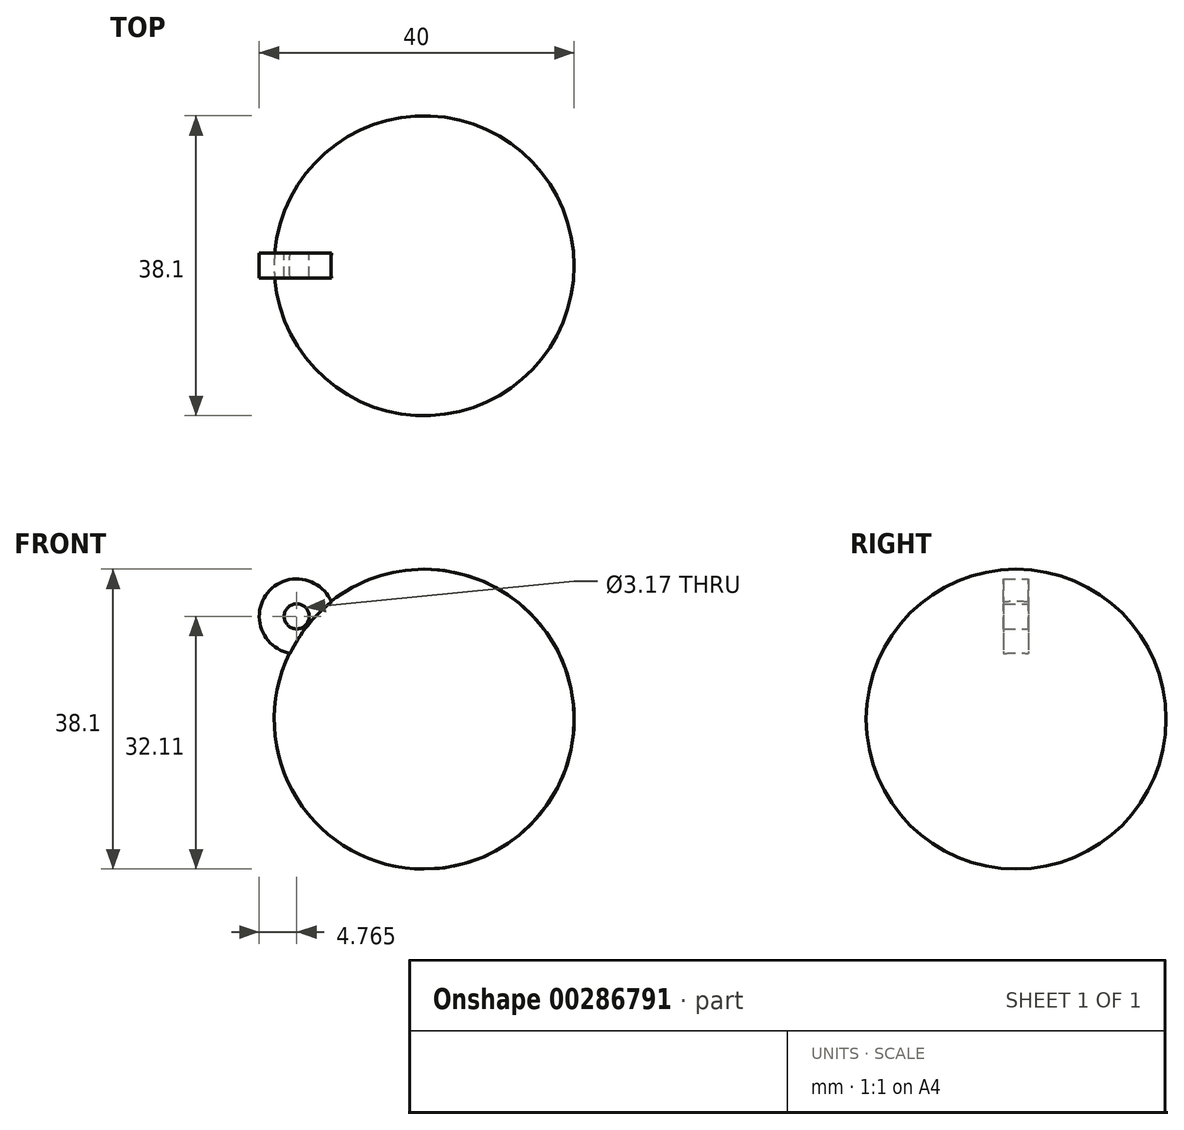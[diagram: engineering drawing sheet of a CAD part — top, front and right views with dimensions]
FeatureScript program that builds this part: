
annotation { "Feature Type Name" : "Feature", "Feature Type Description" : "" }
export const myFeature = defineFeature(function(context is Context, id is Id, definition is map)
    precondition{}
    {
        {
            var Q0;
            Q0=qCreatedBy(makeId("Front.planeOp"),FACE);
            var sketch = newSketch(context, id + "F0", { "sketchPlane" : qUnion([Q0])});
            skArc(sketch, "E0", {"start": v(0, 19.05) * mm, "mid": v(-19.05, 0) * mm, "end": v(0, -19.05) * mm});
            skLineSegment(sketch, "E1", {"start": v(0, 19.05) * mm, "end": v(0, -19.05) * mm});
            skSolve(sketch);
        }
        {
            var Q0;
            Q0=makeQuery(id+"F0.imprint","IMPRINT",FACE,{"disambiguationData":[TD([[makeQuery(id+"F0.imprint","IMPRINT",EDGE,{"derivedFrom":sQuery(id+"F0.wireOp",EDGE,"E0")}),1.0]])]});
            var Q1;
            Q1=sQuery(id+"F0.wireOp",EDGE,"E1");
            revolve(context, id + "F1", {"entities" : qUnion([Q0]), "axis" : qUnion([Q1]), "revolveType" : RevolveType.FULL});
        }
        {
            var Q0;
            Q0=qCreatedBy(makeId("Front.planeOp"),FACE);
            var sketch = newSketch(context, id + "F2", { "sketchPlane" : qUnion([Q0])});
            skCircle(sketch, "E2", {"center": v(-16.19, 13.06) * mm, "radius": 1.59 * mm});
            skCircle(sketch, "E3", {"center": v(-16.19, 13.06) * mm, "radius": 4.76 * mm});
            skSolve(sketch);
        }
        {
            var Q0;
            Q0 = qSketchRegion(id + "F2", true);
            extrude(context, id + "F3", {"entities" : qUnion([Q0]), "operationType" : NewBodyOperationType.ADD, "offsetDistance" : 25.4 * mm, "depth" : 1.59 * mm, "hasSecondDirection" : true, "secondDirectionOppositeDirection" : true, "secondDirectionDepth" : 1.59 * mm});
        }
    });
